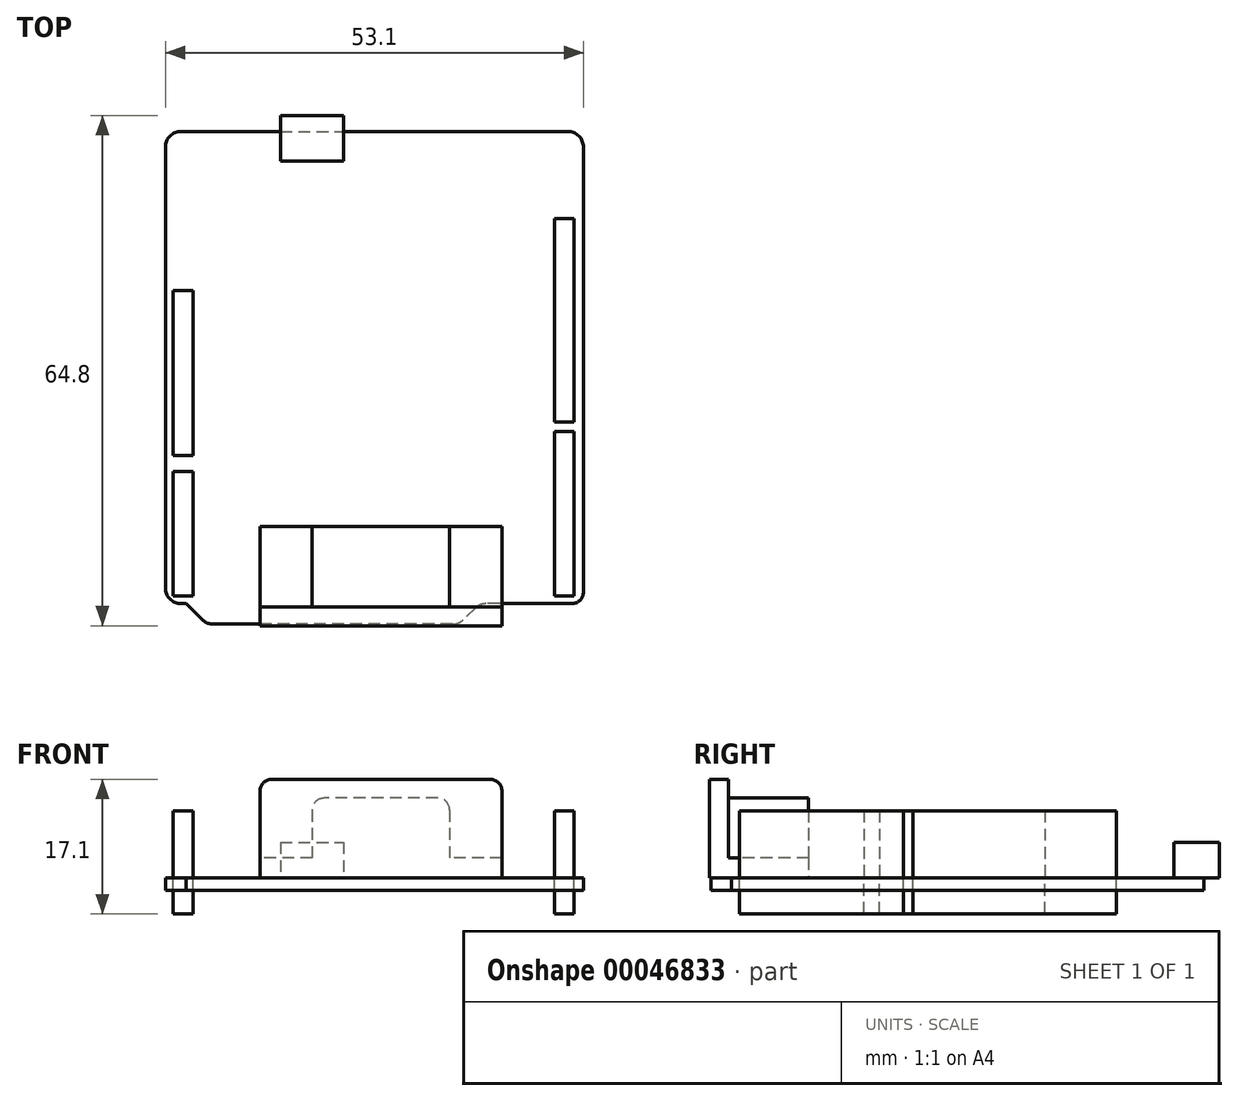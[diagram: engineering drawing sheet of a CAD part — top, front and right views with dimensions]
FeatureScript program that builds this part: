
annotation { "Feature Type Name" : "Feature", "Feature Type Description" : "" }
export const myFeature = defineFeature(function(context is Context, id is Id, definition is map)
    precondition{}
    {
        {
            var Q0;
            Q0=qCreatedBy(makeId("Top.planeOp"),FACE);
            var sketch = newSketch(context, id + "F0", { "sketchPlane" : qUnion([Q0])});
            skLineSegment(sketch, "E0", {"start": v(-21.1, 31.3) * mm, "end": v(28, 31.3) * mm});
            skLineSegment(sketch, "E1", {"start": v(30, 29.3) * mm, "end": v(30, -27.2) * mm});
            skLineSegment(sketch, "E2", {"start": v(28.5, -28.7) * mm, "end": v(17.63, -28.7) * mm});
            skLineSegment(sketch, "E3", {"start": v(16.21, -29.29) * mm, "end": v(14.79, -30.71) * mm});
            skLineSegment(sketch, "E4", {"start": v(13.37, -31.3) * mm, "end": v(-17.02, -31.3) * mm});
            skLineSegment(sketch, "E5", {"start": v(-18.44, -30.71) * mm, "end": v(-20.45, -28.7) * mm});
            skLineSegment(sketch, "E6", {"start": v(-20.45, -28.7) * mm, "end": v(-21.1, -28.7) * mm});
            skLineSegment(sketch, "E7", {"start": v(-23.1, -26.7) * mm, "end": v(-23.1, 29.3) * mm});
            skPoint(sketch, "E8.visualSharp", {"position": v(-23.1, 31.3) * mm});
            skArc(sketch, "E8.filletArc", {"start": v(-21.1, 31.3) * mm, "mid": v(-22.51, 30.71) * mm, "end": v(-23.1, 29.3) * mm});
            skPoint(sketch, "E9.visualSharp", {"position": v(30, 31.3) * mm});
            skArc(sketch, "E9.filletArc", {"start": v(30, 29.3) * mm, "mid": v(29.41, 30.71) * mm, "end": v(28, 31.3) * mm});
            skPoint(sketch, "E10.visualSharp", {"position": v(-23.1, -28.7) * mm});
            skArc(sketch, "E10.filletArc", {"start": v(-23.1, -26.7) * mm, "mid": v(-22.51, -28.11) * mm, "end": v(-21.1, -28.7) * mm});
            skPoint(sketch, "E11.visualSharp", {"position": v(-17.85, -31.3) * mm});
            skArc(sketch, "E11.filletArc", {"start": v(-18.44, -30.71) * mm, "mid": v(-17.79, -31.15) * mm, "end": v(-17.02, -31.3) * mm});
            skPoint(sketch, "E12.visualSharp", {"position": v(14.2, -31.3) * mm});
            skArc(sketch, "E12.filletArc", {"start": v(13.37, -31.3) * mm, "mid": v(14.14, -31.15) * mm, "end": v(14.79, -30.71) * mm});
            skPoint(sketch, "E13.visualSharp", {"position": v(16.8, -28.7) * mm});
            skArc(sketch, "E13.filletArc", {"start": v(17.63, -28.7) * mm, "mid": v(16.86, -28.85) * mm, "end": v(16.21, -29.29) * mm});
            skPoint(sketch, "E14.visualSharp", {"position": v(30, -28.7) * mm});
            skArc(sketch, "E14.filletArc", {"start": v(28.5, -28.7) * mm, "mid": v(29.56, -28.26) * mm, "end": v(30, -27.2) * mm});
            skSolve(sketch);
        }
        {
            var Q0;
            Q0 = qSketchRegion(id + "F0", true);
            extrude(context, id + "F1", {"entities" : qUnion([Q0]), "depth" : 1.6 * mm});
        }
        {
            var Q0;
            Q0=makeQuery(id+"F1.opExtrude","CAP_FACE",FACE,{"disambiguationData":[OSD([sQuery(id+"F0.wireOp",EDGE,"E0"),sQuery(id+"F0.wireOp",EDGE,"E1"),sQuery(id+"F0.wireOp",EDGE,"E2"),sQuery(id+"F0.wireOp",EDGE,"E3"),sQuery(id+"F0.wireOp",EDGE,"E4"),sQuery(id+"F0.wireOp",EDGE,"E5"),sQuery(id+"F0.wireOp",EDGE,"E6"),sQuery(id+"F0.wireOp",EDGE,"E7"),sQuery(id+"F0.wireOp",EDGE,"E8.filletArc"),sQuery(id+"F0.wireOp",EDGE,"E9.filletArc"),sQuery(id+"F0.wireOp",EDGE,"E10.filletArc"),sQuery(id+"F0.wireOp",EDGE,"E11.filletArc"),sQuery(id+"F0.wireOp",EDGE,"E12.filletArc"),sQuery(id+"F0.wireOp",EDGE,"E13.filletArc"),sQuery(id+"F0.wireOp",EDGE,"E14.filletArc")])],"isStart":false});
            var sketch = newSketch(context, id + "F2", { "sketchPlane" : qUnion([Q0])});
            skLineSegment(sketch, "E15.bottom", {"start": v(28.8, 20.2) * mm, "end": v(26.3, 20.2) * mm});
            skLineSegment(sketch, "E15.top", {"start": v(28.8, -5.65) * mm, "end": v(26.3, -5.65) * mm});
            skLineSegment(sketch, "E15.left", {"start": v(28.8, 20.2) * mm, "end": v(28.8, -5.65) * mm});
            skLineSegment(sketch, "E15.right", {"start": v(26.3, 20.2) * mm, "end": v(26.3, -5.65) * mm});
            skLineSegment(sketch, "E16.bottom", {"start": v(28.8, -6.85) * mm, "end": v(26.3, -6.85) * mm});
            skLineSegment(sketch, "E16.top", {"start": v(28.8, -27.7) * mm, "end": v(26.3, -27.7) * mm});
            skLineSegment(sketch, "E16.left", {"start": v(28.8, -6.85) * mm, "end": v(28.8, -27.7) * mm});
            skLineSegment(sketch, "E16.right", {"start": v(26.3, -6.85) * mm, "end": v(26.3, -27.7) * mm});
            skLineSegment(sketch, "E17.bottom", {"start": v(-19.6, 11.1) * mm, "end": v(-22.1, 11.1) * mm});
            skLineSegment(sketch, "E17.top", {"start": v(-19.6, -9.9) * mm, "end": v(-22.1, -9.9) * mm});
            skLineSegment(sketch, "E17.left", {"start": v(-19.6, 11.1) * mm, "end": v(-19.6, -9.9) * mm});
            skLineSegment(sketch, "E17.right", {"start": v(-22.1, 11.1) * mm, "end": v(-22.1, -9.9) * mm});
            skLineSegment(sketch, "E18.bottom", {"start": v(-19.6, -11.9) * mm, "end": v(-22.1, -11.9) * mm});
            skLineSegment(sketch, "E18.top", {"start": v(-19.6, -27.7) * mm, "end": v(-22.1, -27.7) * mm});
            skLineSegment(sketch, "E18.left", {"start": v(-19.6, -11.9) * mm, "end": v(-19.6, -27.7) * mm});
            skLineSegment(sketch, "E18.right", {"start": v(-22.1, -11.9) * mm, "end": v(-22.1, -27.7) * mm});
            skSolve(sketch);
        }
        {
            var Q0;
            Q0 = qSketchRegion(id + "F2", true);
            extrude(context, id + "F3", {"entities" : qUnion([Q0]), "depth" : 8.5 * mm});
        }
        {
            var Q0;
            Q0 = qSketchRegion(id + "F2", true);
            extrude(context, id + "F4", {"entities" : qUnion([Q0]), "oppositeDirection" : true, "depth" : 4.6 * mm});
        }
        {
            var Q0;
            Q0=makeQuery(id+"F1.opExtrude","CAP_FACE",FACE,{"disambiguationData":[OSD([sQuery(id+"F0.wireOp",EDGE,"E0"),sQuery(id+"F0.wireOp",EDGE,"E1"),sQuery(id+"F0.wireOp",EDGE,"E2"),sQuery(id+"F0.wireOp",EDGE,"E3"),sQuery(id+"F0.wireOp",EDGE,"E4"),sQuery(id+"F0.wireOp",EDGE,"E5"),sQuery(id+"F0.wireOp",EDGE,"E6"),sQuery(id+"F0.wireOp",EDGE,"E7"),sQuery(id+"F0.wireOp",EDGE,"E8.filletArc"),sQuery(id+"F0.wireOp",EDGE,"E9.filletArc"),sQuery(id+"F0.wireOp",EDGE,"E10.filletArc"),sQuery(id+"F0.wireOp",EDGE,"E11.filletArc"),sQuery(id+"F0.wireOp",EDGE,"E12.filletArc"),sQuery(id+"F0.wireOp",EDGE,"E13.filletArc"),sQuery(id+"F0.wireOp",EDGE,"E14.filletArc")])],"isStart":false});
            var sketch = newSketch(context, id + "F5", { "sketchPlane" : qUnion([Q0])});
            skLineSegment(sketch, "E19.bottom", {"start": v(-8.5, 27.5) * mm, "end": v(-0.5, 27.5) * mm});
            skLineSegment(sketch, "E19.top", {"start": v(-8.5, 33.3) * mm, "end": v(-0.5, 33.3) * mm});
            skLineSegment(sketch, "E19.left", {"start": v(-8.5, 27.5) * mm, "end": v(-8.5, 33.3) * mm});
            skLineSegment(sketch, "E19.right", {"start": v(-0.5, 27.5) * mm, "end": v(-0.5, 33.3) * mm});
            skSolve(sketch);
        }
        {
            var Q0;
            Q0 = qSketchRegion(id + "F5", true);
            extrude(context, id + "F6", {"entities" : qUnion([Q0]), "depth" : 4.5 * mm});
        }
        {
            var Q0;
            Q0=makeQuery(id+"F1.opExtrude","CAP_FACE",FACE,{"disambiguationData":[OSD([sQuery(id+"F0.wireOp",EDGE,"E0"),sQuery(id+"F0.wireOp",EDGE,"E1"),sQuery(id+"F0.wireOp",EDGE,"E2"),sQuery(id+"F0.wireOp",EDGE,"E3"),sQuery(id+"F0.wireOp",EDGE,"E4"),sQuery(id+"F0.wireOp",EDGE,"E5"),sQuery(id+"F0.wireOp",EDGE,"E6"),sQuery(id+"F0.wireOp",EDGE,"E7"),sQuery(id+"F0.wireOp",EDGE,"E8.filletArc"),sQuery(id+"F0.wireOp",EDGE,"E9.filletArc"),sQuery(id+"F0.wireOp",EDGE,"E10.filletArc"),sQuery(id+"F0.wireOp",EDGE,"E11.filletArc"),sQuery(id+"F0.wireOp",EDGE,"E12.filletArc"),sQuery(id+"F0.wireOp",EDGE,"E13.filletArc"),sQuery(id+"F0.wireOp",EDGE,"E14.filletArc")])],"isStart":false});
            var sketch = newSketch(context, id + "F7", { "sketchPlane" : qUnion([Q0])});
            skLineSegment(sketch, "E20.bottom", {"start": v(19.65, -18.9) * mm, "end": v(-11.1, -18.9) * mm});
            skLineSegment(sketch, "E20.top", {"start": v(19.65, -31.5) * mm, "end": v(-11.1, -31.5) * mm});
            skLineSegment(sketch, "E20.left", {"start": v(19.65, -18.9) * mm, "end": v(19.65, -31.5) * mm});
            skLineSegment(sketch, "E20.right", {"start": v(-11.1, -18.9) * mm, "end": v(-11.1, -31.5) * mm});
            skSolve(sketch);
        }
        {
            var Q0;
            Q0 = qSketchRegion(id + "F7", true);
            extrude(context, id + "F8", {"entities" : qUnion([Q0]), "operationType" : NewBodyOperationType.ADD, "depth" : 12.5 * mm});
        }
        {
            var Q0;
            Q0=makeQuery(id+"F8.opExtrude","CAP_FACE",FACE,{"disambiguationData":[OSD([sQuery(id+"F7.wireOp",EDGE,"E20.bottom"),sQuery(id+"F7.wireOp",EDGE,"E20.top"),sQuery(id+"F7.wireOp",EDGE,"E20.left"),sQuery(id+"F7.wireOp",EDGE,"E20.right")])],"isStart":false});
            var sketch = newSketch(context, id + "F9", { "sketchPlane" : qUnion([Q0])});
            skLineSegment(sketch, "E21.bottom", {"start": v(19.65, -18.9) * mm, "end": v(-11.1, -18.9) * mm});
            skLineSegment(sketch, "E21.top", {"start": v(19.65, -29.1) * mm, "end": v(-11.1, -29.1) * mm});
            skLineSegment(sketch, "E21.left", {"start": v(19.65, -18.9) * mm, "end": v(19.65, -29.1) * mm});
            skLineSegment(sketch, "E21.right", {"start": v(-11.1, -18.9) * mm, "end": v(-11.1, -29.1) * mm});
            skSolve(sketch);
        }
        {
            var Q0;
            Q0 = qSketchRegion(id + "F9", true);
            extrude(context, id + "F10", {"entities" : qUnion([Q0]), "operationType" : NewBodyOperationType.REMOVE, "oppositeDirection" : true, "depth" : 10 * mm});
        }
        {
            var Q0;
            Q0=makeQuery(id+"F10.boolean.opBoolean","COPY",FACE,{"derivedFrom":makeQuery(id+"F10.opExtrude","CAP_FACE",FACE,{"disambiguationData":[OSD([sQuery(id+"F9.wireOp",EDGE,"E21.bottom"),sQuery(id+"F9.wireOp",EDGE,"E21.top"),sQuery(id+"F9.wireOp",EDGE,"E21.left"),sQuery(id+"F9.wireOp",EDGE,"E21.right")])],"isStart":false})});
            var sketch = newSketch(context, id + "F11", { "sketchPlane" : qUnion([Q0])});
            skLineSegment(sketch, "E22.bottom", {"start": v(13, -18.9) * mm, "end": v(-4.45, -18.9) * mm});
            skLineSegment(sketch, "E22.top", {"start": v(13, -29.1) * mm, "end": v(-4.45, -29.1) * mm});
            skLineSegment(sketch, "E22.left", {"start": v(13, -18.9) * mm, "end": v(13, -29.1) * mm});
            skLineSegment(sketch, "E22.right", {"start": v(-4.45, -18.9) * mm, "end": v(-4.45, -29.1) * mm});
            skSolve(sketch);
        }
        {
            var Q0;
            Q0 = qSketchRegion(id + "F11", true);
            extrude(context, id + "F12", {"entities" : qUnion([Q0]), "operationType" : NewBodyOperationType.ADD, "depth" : 7.6 * mm});
        }
        {
            var Q0;
            Q0=makeQuery(id+"F12.opExtrude","CAP_EDGE",EDGE,{"disambiguationData":[OSD([sQuery(id+"F11.wireOp",EDGE,"E22.right")])],"isStart":false});
            var Q1;
            Q1=makeQuery(id+"F12.opExtrude","CAP_EDGE",EDGE,{"disambiguationData":[OSD([sQuery(id+"F11.wireOp",EDGE,"E22.left")])],"isStart":false});
            var Q2;
            Q2=makeQuery(id+"F8.opExtrude","CAP_EDGE",EDGE,{"disambiguationData":[OSD([sQuery(id+"F7.wireOp",EDGE,"E20.left")])],"isStart":false});
            var Q3;
            Q3=makeQuery(id+"F8.opExtrude","CAP_EDGE",EDGE,{"disambiguationData":[OSD([sQuery(id+"F7.wireOp",EDGE,"E20.right")])],"isStart":false});
            fillet(context, id + "F13", {"entities" : qUnion([Q0, Q1, Q2, Q3]), "radius" : 1.5 * mm, "tangentPropagation" : true, "allowEdgeOverflow" : false});
        }
    });
